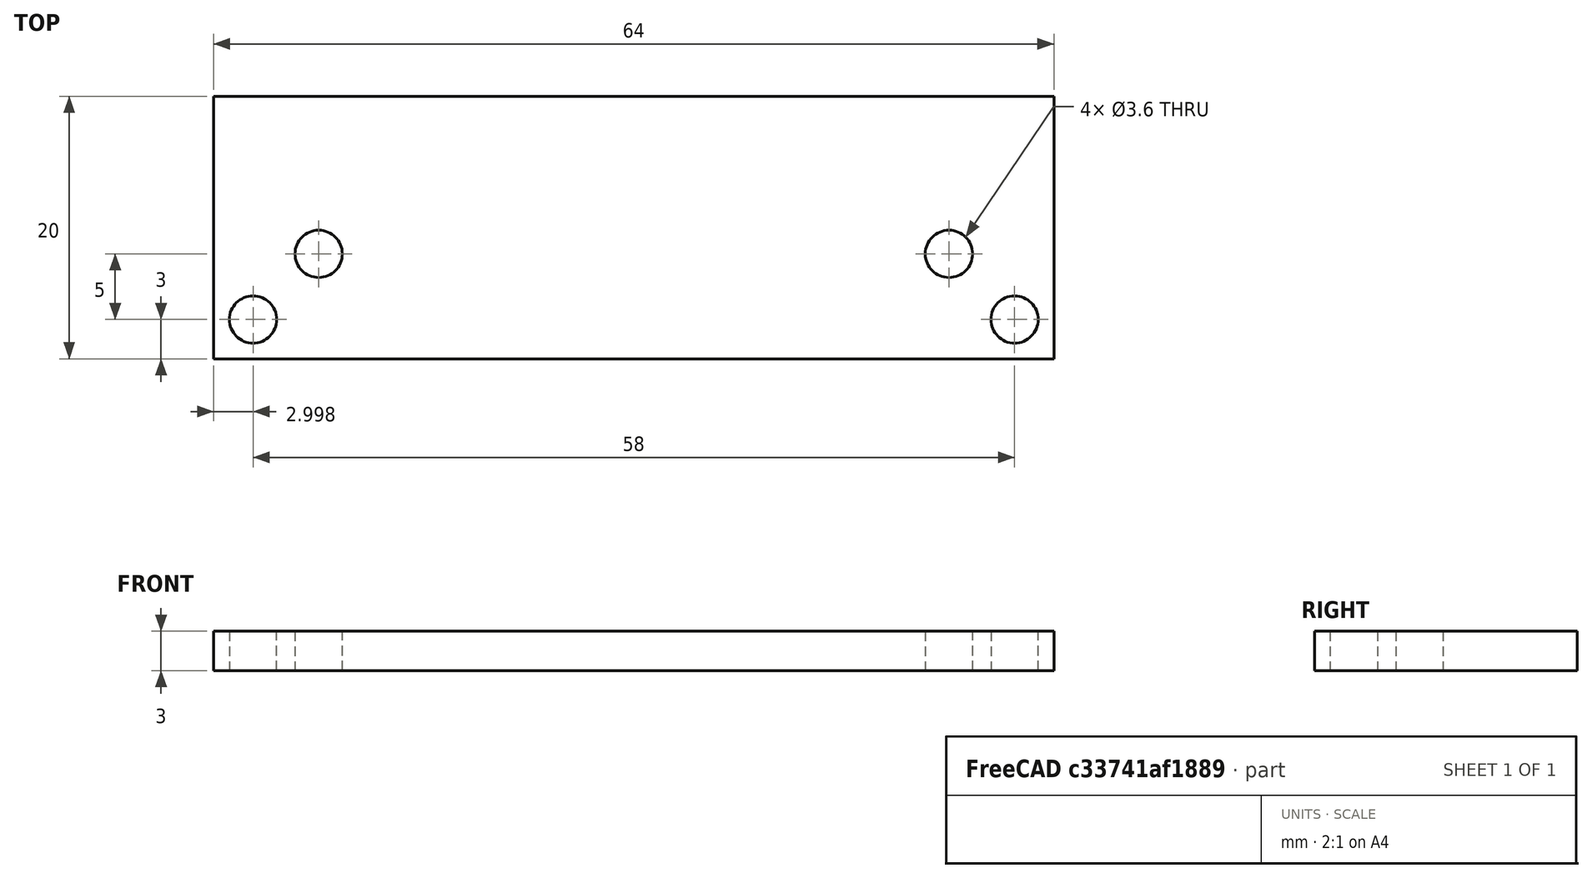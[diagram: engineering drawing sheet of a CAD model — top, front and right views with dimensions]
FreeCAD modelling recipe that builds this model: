
FCSTD DOCUMENT  (FreeCAD 0.21R33668 +26 (Git))
Label: arduino_holder
License: All rights reserved
LicenseURL: https://en.wikipedia.org/wiki/All_rights_reserved
objects: Sketcher::SketchObject×1, PartDesign::Pad×1, PartDesign::Body×1
note: 4 computed .brp shape members not serialized (recipe doc carries the construction recipe); baked Part::Feature solids carry a one-line shape summary decoded from their .brp

FEATURE [Sketcher::SketchObject] Sketch
  FullyConstrained = false
  MapMode = 5
  Support = -> [XY_Plane]
  sketch-geometry (25):
    g0: LineSegment StartX=131.708 StartY=13.9896 StartZ=0 EndX=189.708 EndY=13.9896 EndZ=0
    g1: LineSegment StartX=189.708 StartY=13.9896 StartZ=0 EndX=189.708 EndY=-35.0104 EndZ=0
    g2: LineSegment StartX=189.708 StartY=-35.0104 StartZ=0 EndX=131.708 EndY=-35.0104 EndZ=0
    g3: LineSegment StartX=131.708 StartY=-35.0104 StartZ=0 EndX=131.708 EndY=13.9896 EndZ=0
    g4: Circle CenterX=131.708 CenterY=13.9896 CenterZ=0 NormalX=0 NormalY=0 NormalZ=1 AngleXU=0 Radius=1.8
    g5: Circle CenterX=131.708 CenterY=-35.0104 CenterZ=0 NormalX=0 NormalY=0 NormalZ=1 AngleXU=0 Radius=1.8
    g6: Circle CenterX=189.708 CenterY=-35.0104 CenterZ=0 NormalX=0 NormalY=0 NormalZ=1 AngleXU=0 Radius=1.8
    g7: Circle CenterX=189.708 CenterY=13.9896 CenterZ=0 NormalX=0 NormalY=0 NormalZ=1 AngleXU=0 Radius=1.8
    g8: GeomPoint X=132.485 Y=12.3661 Z=0
    g9: GeomPoint X=190.704 Y=12.4905 Z=0
    g10: GeomPoint X=132.434 Y=-36.6576 Z=0
    g11: GeomPoint X=190.643 Y=-36.5483 Z=0
    g12: Circle CenterX=184.708 CenterY=-30.0104 CenterZ=0 NormalX=0 NormalY=0 NormalZ=1 AngleXU=0 Radius=1.8
    g13: Circle CenterX=136.708 CenterY=-30.0104 CenterZ=0 NormalX=0 NormalY=0 NormalZ=1 AngleXU=0 Radius=1.8
    g14: GeomPoint X=184.374 Y=-31.7791 Z=0
    g15: GeomPoint X=138.352 Y=-30.7437 Z=0
    g16: LineSegment StartX=192.708 StartY=-38.0104 StartZ=0 EndX=128.708 EndY=-38.0104 EndZ=0
    g17: LineSegment StartX=131.708 StartY=13.9896 StartZ=0 EndX=129.485 EndY=13.9896 EndZ=0
    g18: LineSegment StartX=131.708 StartY=-35.0104 StartZ=0 EndX=128.708 EndY=-35.0104 EndZ=0
    g19: LineSegment StartX=128.708 StartY=-38.0104 StartZ=0 EndX=128.708 EndY=-18.0104 EndZ=0
    g20: LineSegment StartX=128.708 StartY=-18.0104 StartZ=0 EndX=192.708 EndY=-18.0104 EndZ=0
    g21: LineSegment StartX=192.708 StartY=-18.0104 StartZ=0 EndX=192.708 EndY=-38.0104 EndZ=0
    g22: LineSegment StartX=136.708 StartY=-30.0104 StartZ=0 EndX=184.708 EndY=-30.0104 EndZ=0
    g23: LineSegment StartX=160.708 StartY=-30.0104 StartZ=0 EndX=160.708 EndY=-35.0104 EndZ=0
    g24: LineSegment StartX=189.708 StartY=-35.0104 StartZ=0 EndX=192.708 EndY=-35.0104 EndZ=0
  constraints (56):
    c: Coincident(g0,g1)
    c: Coincident(g1,g2)
    c: Coincident(g2,g3)
    c: Coincident(g3,g0)
    c: Horizontal(g0)
    c: Horizontal(g2)
    c: Vertical(g1)
    c: Vertical(g3)
    c: Distance(g1) = 49
    c: Distance(g0) = 58
    c: Coincident(g4,g0)
    c: Coincident(g5,g2)
    c: Coincident(g6,g1)
    c: Coincident(g7,g0)
    c: PointOnObject(g8,g4)
    c: PointOnObject(g9,g7)
    c: PointOnObject(g10,g5)
    c: PointOnObject(g11,g6)
    c: Distance(g8,g0) = 1.8
    c: Distance(g9,g0) = 1.8
    c: Distance(g2,g10) = 1.8
    c: Distance(g11,g1) = 1.8
    c: PointOnObject(g14,g12)
    c: PointOnObject(g15,g13)
    c: Distance(g14,g12) = 1.8
    c: Distance(g15,g13) = 1.8
    c: Horizontal(g16)
    c: Coincident(g17,g4)
    c: Horizontal(g17)
    c: Coincident(g18,g5)
    c: Horizontal(g18)
    c: Distance(g18) = 3
    c: Coincident(g19,g16)
    c: Vertical(g19)
    c: Coincident(g20,g19)
    c: Horizontal(g20)
    c: Coincident(g21,g20)
    c: Coincident(g21,g16)
    c: Vertical(g21)
    c: Coincident(g22,g13)
    c: Coincident(g22,g12)
    c: Horizontal(g22)
    c: PointOnObject(g23,g22)
    c: PointOnObject(g23,g2)
    c: Vertical(g23)
    c: Distance(g22) = 48
    c: Distance(g13,g23) = 24
    c: Distance(g5,g23) = 29
    c: Distance(g23) = 5
    c: PointOnObject(g18,g19)
    c: Distance(g16,g18) = 3
    c: Coincident(g24,g6)
    c: PointOnObject(g24,g21)
    c: Horizontal(g24)
    c: Distance(g24) = 3
    c: Distance(g19) = 20
FEATURE [PartDesign::Pad] Pad
  Direction = (0,0,1)
  Length = 3
  Length2 = 10
  Profile = -> Sketch
  ReferenceAxis = -> Sketch [N_Axis]
  Type = 0
FEATURE [PartDesign::Body] Body
  Group = -> [Sketch,Pad]
  Origin = -> Origin
  Tip = -> Pad
